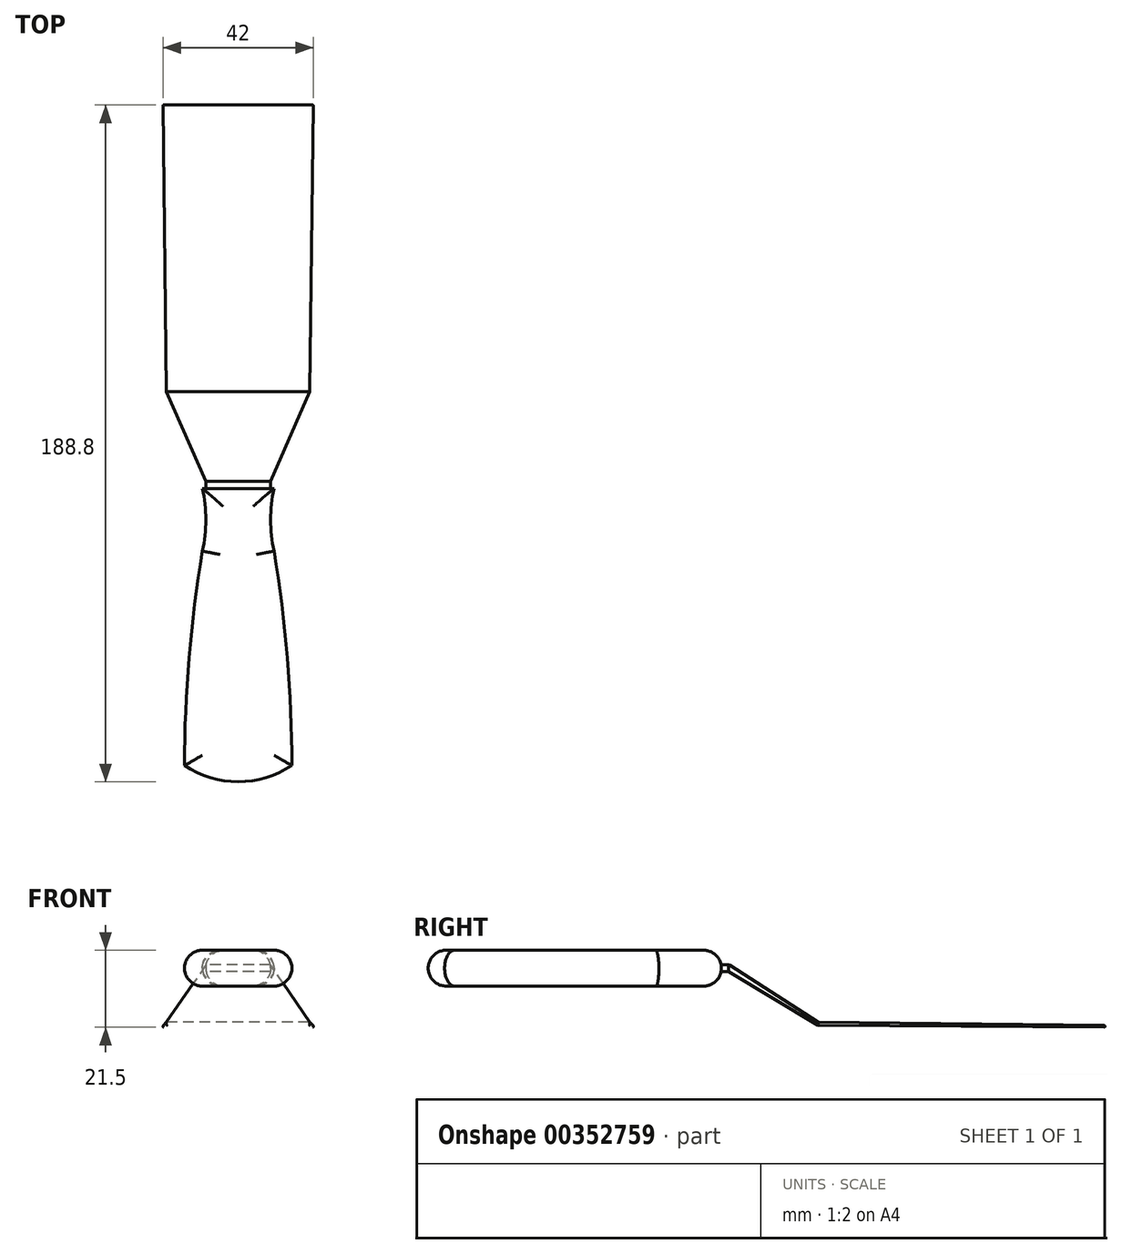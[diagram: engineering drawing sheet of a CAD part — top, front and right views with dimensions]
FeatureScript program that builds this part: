
annotation { "Feature Type Name" : "Feature", "Feature Type Description" : "" }
export const myFeature = defineFeature(function(context is Context, id is Id, definition is map)
    precondition{}
    {
        {
            var Q0;
            Q0=qCreatedBy(makeId("Top.planeOp"),FACE);
            var sketch = newSketch(context, id + "F0", { "sketchPlane" : qUnion([Q0])});
            skLineSegment(sketch, "E0", {"start": v(-10, 15) * mm, "end": v(10, 15) * mm});
            skArc(sketch, "E1", {"start": v(10, 15) * mm, "mid": v(9.03, 6.28) * mm, "end": v(10, -2.44) * mm});
            skArc(sketch, "E2", {"start": v(15, -62.2) * mm, "mid": v(13.7, -32.23) * mm, "end": v(10, -2.44) * mm});
            skArc(sketch, "E3", {"start": v(-15, -62.2) * mm, "mid": v(0, -66.8) * mm, "end": v(15, -62.2) * mm});
            skLineSegment(sketch, "E4", {"start": v(0, 56.86) * mm, "end": v(0, -79.19) * mm, "construction": true});
            skArc(sketch, "E5.MirrorCS", {"start": v(-10, 15) * mm, "mid": v(-9.03, 6.28) * mm, "end": v(-10, -2.44) * mm});
            skArc(sketch, "E6.MirrorCS", {"start": v(-15, -62.2) * mm, "mid": v(-13.7, -32.23) * mm, "end": v(-10, -2.44) * mm});
            skSolve(sketch);
        }
        {
            var Q0;
            Q0=makeQuery(id+"F0.imprint","IMPRINT",FACE,{"disambiguationData":[TD([[makeQuery(id+"F0.imprint","IMPRINT",EDGE,{"derivedFrom":sQuery(id+"F0.wireOp",EDGE,"E0")}),-1.0]])]});
            extrude(context, id + "F1", {"entities" : qUnion([Q0]), "endBound" : BoundingType.SYMMETRIC, "depth" : 10 * mm});
        }
        {
            var Q0;
            Q0=makeQuery(id+"F1.opExtrude","CAP_EDGE",EDGE,{"disambiguationData":[OSD([sQuery(id+"F0.wireOp",EDGE,"E5.MirrorCS")])],"isStart":false});
            var Q1;
            Q1=makeQuery(id+"F1.opExtrude","CAP_EDGE",EDGE,{"disambiguationData":[OSD([sQuery(id+"F0.wireOp",EDGE,"E6.MirrorCS")])],"isStart":false});
            var Q2;
            Q2=makeQuery(id+"F1.opExtrude","CAP_EDGE",EDGE,{"disambiguationData":[OSD([sQuery(id+"F0.wireOp",EDGE,"E3")])],"isStart":false});
            var Q3;
            Q3=makeQuery(id+"F1.opExtrude","CAP_FACE",FACE,{"disambiguationData":[OSD([sQuery(id+"F0.wireOp",EDGE,"E0"),sQuery(id+"F0.wireOp",EDGE,"E1"),sQuery(id+"F0.wireOp",EDGE,"E2"),sQuery(id+"F0.wireOp",EDGE,"E3"),sQuery(id+"F0.wireOp",EDGE,"E5.MirrorCS"),sQuery(id+"F0.wireOp",EDGE,"E6.MirrorCS")])],"isStart":false});
            var Q4;
            Q4=makeQuery(id+"F1.opExtrude","CAP_EDGE",EDGE,{"disambiguationData":[OSD([sQuery(id+"F0.wireOp",EDGE,"E2")])],"isStart":true});
            var Q5;
            Q5=makeQuery(id+"F1.opExtrude","CAP_EDGE",EDGE,{"disambiguationData":[OSD([sQuery(id+"F0.wireOp",EDGE,"E0")])],"isStart":true});
            var Q6;
            Q6=makeQuery(id+"F1.opExtrude","CAP_EDGE",EDGE,{"disambiguationData":[OSD([sQuery(id+"F0.wireOp",EDGE,"E5.MirrorCS")])],"isStart":true});
            var Q7;
            Q7=makeQuery(id+"F1.opExtrude","CAP_EDGE",EDGE,{"disambiguationData":[OSD([sQuery(id+"F0.wireOp",EDGE,"E6.MirrorCS")])],"isStart":true});
            var Q8;
            Q8=makeQuery(id+"F1.opExtrude","CAP_EDGE",EDGE,{"disambiguationData":[OSD([sQuery(id+"F0.wireOp",EDGE,"E3")])],"isStart":true});
            fillet(context, id + "F2", {"entities" : qUnion([Q0, Q1, Q2, Q3, Q4, Q5, Q6, Q7, Q8]), "radius" : 5 * mm, "tangentPropagation" : true, "allowEdgeOverflow" : false});
        }
        {
            var Q0;
            Q0=qCreatedBy(makeId("Front.planeOp"),FACE);
            cPlane(context, id + "F3", {"entities" : qUnion([Q0]), "cplaneType" : CPlaneType.OFFSET, "offset" : 15 * mm, "oppositeDirection" : true, "width" : 150 * mm, "height" : 150 * mm});
        }
        {
            var Q0;
            Q0=qCreatedBy(id+"F3.planeOp",FACE);
            var sketch = newSketch(context, id + "F4", { "sketchPlane" : qUnion([Q0])});
            skLineSegment(sketch, "E7.bottom", {"start": v(9, 1) * mm, "end": v(-9, 1) * mm});
            skLineSegment(sketch, "E7.top", {"start": v(9, -1) * mm, "end": v(-9, -1) * mm});
            skLineSegment(sketch, "E7.left", {"start": v(9, 1) * mm, "end": v(9, -1) * mm});
            skLineSegment(sketch, "E7.right", {"start": v(-9, 1) * mm, "end": v(-9, -1) * mm});
            skSolve(sketch);
        }
        {
            var Q0;
            Q0=qCreatedBy(id+"F3.planeOp",FACE);
            cPlane(context, id + "F5", {"entities" : qUnion([Q0]), "cplaneType" : CPlaneType.OFFSET, "offset" : 2 * mm, "oppositeDirection" : true, "width" : 150 * mm, "height" : 150 * mm});
        }
        {
            var Q0;
            Q0=qCreatedBy(id+"F5.planeOp",FACE);
            var sketch = newSketch(context, id + "F6", { "sketchPlane" : qUnion([Q0])});
            skLineSegment(sketch, "E8.bottom", {"start": v(9, 1) * mm, "end": v(-9, 1) * mm});
            skLineSegment(sketch, "E8.top", {"start": v(9, -1) * mm, "end": v(-9, -1) * mm});
            skLineSegment(sketch, "E8.left", {"start": v(9, 1) * mm, "end": v(9, -1) * mm});
            skLineSegment(sketch, "E8.right", {"start": v(-9, 1) * mm, "end": v(-9, -1) * mm});
            skSolve(sketch);
        }
        {
            var Q0;
            Q0=makeQuery(id+"F4.imprint","IMPRINT",FACE,{"disambiguationData":[TD([[makeQuery(id+"F4.imprint","IMPRINT",EDGE,{"derivedFrom":sQuery(id+"F4.wireOp",EDGE,"E7.bottom")}),1.0]])]});
            var Q1;
            Q1=makeQuery(id+"F6.imprint","IMPRINT",FACE,{"disambiguationData":[TD([[makeQuery(id+"F6.imprint","IMPRINT",EDGE,{"derivedFrom":sQuery(id+"F6.wireOp",EDGE,"E8.bottom")}),1.0]])]});
            loft(context, id + "F7", {"sheetProfilesArray" : [{ "sheetProfileEntities" : qUnion([Q0]) }, { "sheetProfileEntities" : qUnion([Q1]) }]});
        }
        {
            var Q0;
            Q0=qCreatedBy(id+"F5.planeOp",FACE);
            cPlane(context, id + "F8", {"entities" : qUnion([Q0]), "cplaneType" : CPlaneType.OFFSET, "offset" : 25 * mm, "oppositeDirection" : true, "width" : 150 * mm, "height" : 150 * mm});
        }
        {
            var Q0;
            Q0=qCreatedBy(id+"F8.planeOp",FACE);
            var sketch = newSketch(context, id + "F9", { "sketchPlane" : qUnion([Q0])});
            skLineSegment(sketch, "E9.bottom", {"start": v(20, -15) * mm, "end": v(-20, -15) * mm});
            skLineSegment(sketch, "E9.top", {"start": v(20, -16) * mm, "end": v(-20, -16) * mm});
            skLineSegment(sketch, "E9.left", {"start": v(20, -15) * mm, "end": v(20, -16) * mm});
            skLineSegment(sketch, "E9.right", {"start": v(-20, -15) * mm, "end": v(-20, -16) * mm});
            skSolve(sketch);
        }
        {
            var Q1;
            Q1=makeQuery(id+"F7.opLoft","CAP_FACE",FACE,{"disambiguationData":[OSD([makeQuery(id+"F6.imprint","IMPRINT",FACE,{"disambiguationData":[TD([[makeQuery(id+"F6.imprint","IMPRINT",EDGE,{"derivedFrom":sQuery(id+"F6.wireOp",EDGE,"E8.bottom")}),1.0]])]})])],"isStart":true});
            var Q2;
            Q2=makeQuery(id+"F9.imprint","IMPRINT",FACE,{"disambiguationData":[TD([[makeQuery(id+"F9.imprint","IMPRINT",EDGE,{"derivedFrom":sQuery(id+"F9.wireOp",EDGE,"E9.bottom")}),1.0]])]});
            loft(context, id + "F10", {"operationType" : NewBodyOperationType.ADD, "sheetProfilesArray" : [{ "sheetProfileEntities" : qUnion([Q1]) }, { "sheetProfileEntities" : qUnion([Q2]) }]});
        }
        {
            var Q0;
            Q0=qCreatedBy(id+"F8.planeOp",FACE);
            cPlane(context, id + "F11", {"entities" : qUnion([Q0]), "cplaneType" : CPlaneType.OFFSET, "offset" : 80 * mm, "oppositeDirection" : true, "width" : 150 * mm, "height" : 150 * mm});
        }
        {
            var Q0;
            Q0=qCreatedBy(id+"F11.planeOp",FACE);
            var sketch = newSketch(context, id + "F12", { "sketchPlane" : qUnion([Q0])});
            skLineSegment(sketch, "E10.bottom", {"start": v(21, -16) * mm, "end": v(-21, -16) * mm});
            skLineSegment(sketch, "E10.top", {"start": v(21, -16.5) * mm, "end": v(-21, -16.5) * mm});
            skLineSegment(sketch, "E10.left", {"start": v(21, -16) * mm, "end": v(21, -16.5) * mm});
            skLineSegment(sketch, "E10.right", {"start": v(-21, -16) * mm, "end": v(-21, -16.5) * mm});
            skSolve(sketch);
        }
        {
            var Q1;
            Q1=makeQuery(id+"F12.imprint","IMPRINT",FACE,{"disambiguationData":[TD([[makeQuery(id+"F12.imprint","IMPRINT",EDGE,{"derivedFrom":sQuery(id+"F12.wireOp",EDGE,"E10.bottom")}),1.0]])]});
            var Q2;
            Q2=makeQuery(id+"F10.opLoft","CAP_FACE",FACE,{"disambiguationData":[OSD([makeQuery(id+"F9.imprint","IMPRINT",FACE,{"disambiguationData":[TD([[makeQuery(id+"F9.imprint","IMPRINT",EDGE,{"derivedFrom":sQuery(id+"F9.wireOp",EDGE,"E9.bottom")}),1.0]])]})])],"isStart":true});
            loft(context, id + "F13", {"operationType" : NewBodyOperationType.ADD, "sheetProfilesArray" : [{ "sheetProfileEntities" : qUnion([Q1]) }, { "sheetProfileEntities" : qUnion([Q2]) }]});
        }
        {
            var Q0;
            Q0=makeQuery(id+"F13.opLoft","MID_CAP_EDGE",EDGE,{"disambiguationData":[OSD([sQuery(id+"F12.wireOp",EDGE,"E10.bottom"),sQuery(id+"F12.wireOp",EDGE,"E10.left"),sQuery(id+"F12.wireOp",EDGE,"E10.right")])],"capPos":0.0});
            var Q1;
            Q1=makeQuery(id+"F13.opLoft","MID_CAP_EDGE",EDGE,{"disambiguationData":[OSD([sQuery(id+"F12.wireOp",EDGE,"E10.top"),sQuery(id+"F12.wireOp",EDGE,"E10.left"),sQuery(id+"F12.wireOp",EDGE,"E10.right")])],"capPos":0.0});
            fillet(context, id + "F14", {"entities" : qUnion([Q0, Q1]), "radius" : 0.25 * mm, "tangentPropagation" : true, "allowEdgeOverflow" : false});
        }
        {
            var Q0;
            Q0=makeQuery(id+"F13.opLoft","SWEPT_EDGE",EDGE,{"disambiguationData":[OSD([sQuery(id+"F9.wireOp",EDGE,"E9.bottom"),sQuery(id+"F9.wireOp",EDGE,"E9.left"),sQuery(id+"F12.wireOp",EDGE,"E10.bottom"),sQuery(id+"F12.wireOp",EDGE,"E10.left")])]});
            var Q1;
            Q1=makeQuery(id+"F13.opLoft","SWEPT_EDGE",EDGE,{"disambiguationData":[OSD([sQuery(id+"F9.wireOp",EDGE,"E9.top"),sQuery(id+"F9.wireOp",EDGE,"E9.left"),sQuery(id+"F12.wireOp",EDGE,"E10.top"),sQuery(id+"F12.wireOp",EDGE,"E10.left")])]});
            var Q2;
            Q2=makeQuery(id+"F13.opLoft","SWEPT_EDGE",EDGE,{"disambiguationData":[OSD([sQuery(id+"F9.wireOp",EDGE,"E9.bottom"),sQuery(id+"F9.wireOp",EDGE,"E9.right"),sQuery(id+"F12.wireOp",EDGE,"E10.bottom"),sQuery(id+"F12.wireOp",EDGE,"E10.right")])]});
            var Q3;
            Q3=makeQuery(id+"F13.opLoft","SWEPT_EDGE",EDGE,{"disambiguationData":[OSD([sQuery(id+"F9.wireOp",EDGE,"E9.top"),sQuery(id+"F9.wireOp",EDGE,"E9.right"),sQuery(id+"F12.wireOp",EDGE,"E10.top"),sQuery(id+"F12.wireOp",EDGE,"E10.right")])]});
            fillet(context, id + "F15", {"entities" : qUnion([Q0, Q1, Q2, Q3]), "radius" : 0.2 * mm, "tangentPropagation" : true, "allowEdgeOverflow" : false});
        }
        {
            var Q0;
            Q0=makeQuery(id+"F10.opLoft","SWEPT_EDGE",EDGE,{"disambiguationData":[OSD([sQuery(id+"F6.wireOp",EDGE,"E8.bottom"),sQuery(id+"F6.wireOp",EDGE,"E8.right"),sQuery(id+"F9.wireOp",EDGE,"E9.bottom"),sQuery(id+"F9.wireOp",EDGE,"E9.right")])]});
            var Q1;
            Q1=makeQuery(id+"F10.opLoft","SWEPT_EDGE",EDGE,{"disambiguationData":[OSD([sQuery(id+"F6.wireOp",EDGE,"E8.top"),sQuery(id+"F6.wireOp",EDGE,"E8.right"),sQuery(id+"F9.wireOp",EDGE,"E9.top"),sQuery(id+"F9.wireOp",EDGE,"E9.right")])]});
            var Q2;
            Q2=makeQuery(id+"F10.opLoft","SWEPT_EDGE",EDGE,{"disambiguationData":[OSD([sQuery(id+"F6.wireOp",EDGE,"E8.top"),sQuery(id+"F6.wireOp",EDGE,"E8.left"),sQuery(id+"F9.wireOp",EDGE,"E9.top"),sQuery(id+"F9.wireOp",EDGE,"E9.left")])]});
            var Q3;
            Q3=makeQuery(id+"F10.opLoft","SWEPT_EDGE",EDGE,{"disambiguationData":[OSD([sQuery(id+"F6.wireOp",EDGE,"E8.bottom"),sQuery(id+"F6.wireOp",EDGE,"E8.left"),sQuery(id+"F9.wireOp",EDGE,"E9.bottom"),sQuery(id+"F9.wireOp",EDGE,"E9.left")])]});
            var Q4;
            {var subQ0=sQuery(id+"F9.wireOp",EDGE,"E9.right");var subQ1=sQuery(id+"F9.wireOp",EDGE,"E9.left");var subQ2=sQuery(id+"F9.wireOp",EDGE,"E9.top");Q4=makeQuery(id+"F13.boolean.opBoolean","MERGE",EDGE,{"derivedFrom":[makeQuery(id+"F10.opLoft","MID_CAP_EDGE",EDGE,{"disambiguationData":[OSD([subQ2,subQ1,subQ0])],"capPos":1.0}),makeQuery(id+"F13.opLoft","MID_CAP_EDGE",EDGE,{"disambiguationData":[OSD([subQ2,subQ1,subQ0])],"capPos":1.0})]});}
            fillet(context, id + "F16", {"entities" : qUnion([Q0, Q1, Q2, Q3, Q4]), "radius" : 0.1 * mm, "tangentPropagation" : true, "allowEdgeOverflow" : false});
        }
    });
